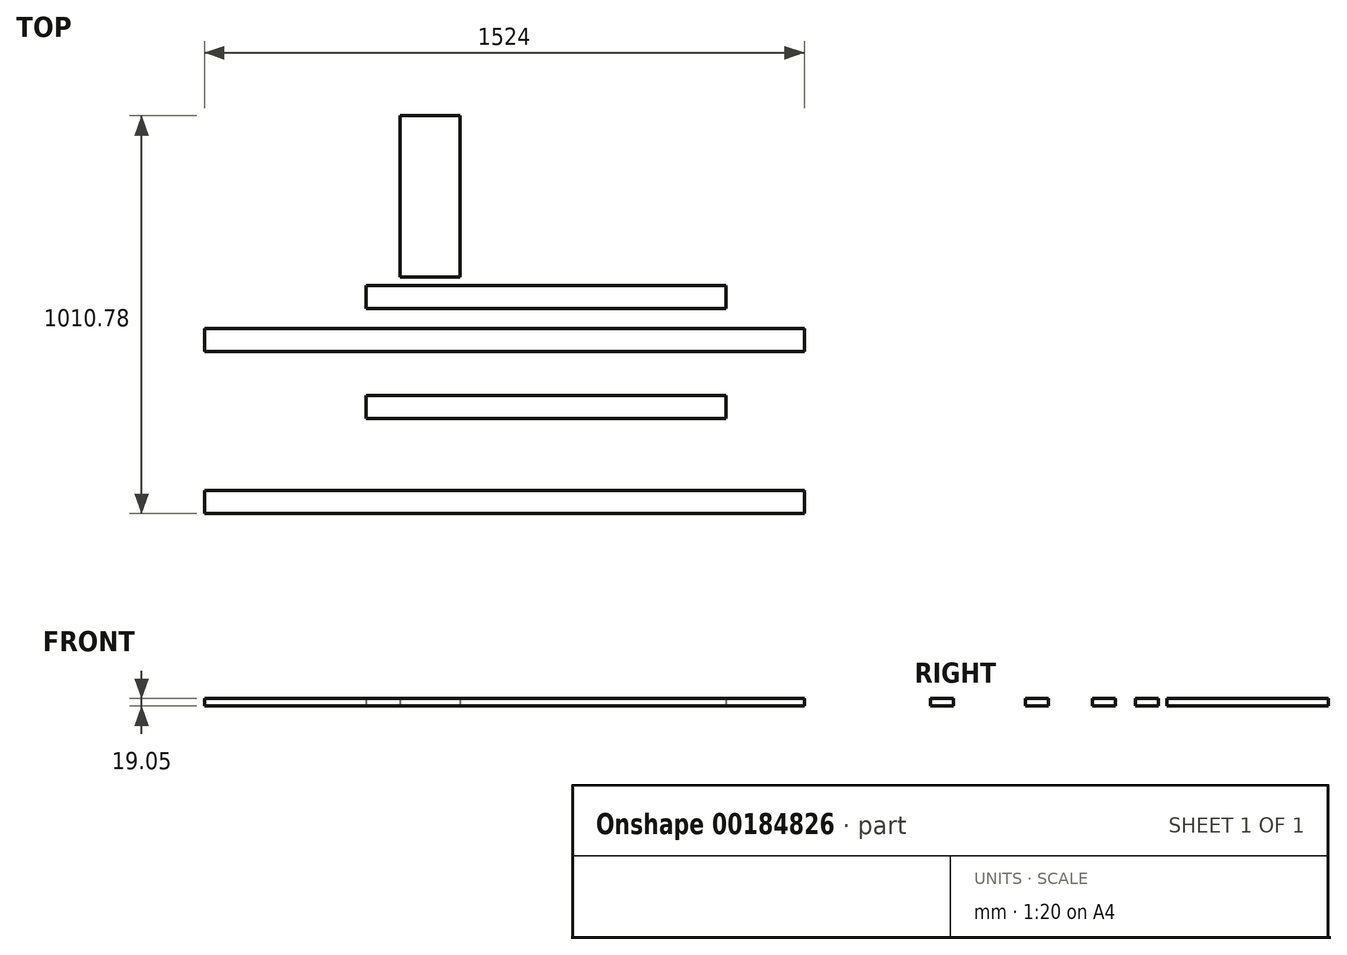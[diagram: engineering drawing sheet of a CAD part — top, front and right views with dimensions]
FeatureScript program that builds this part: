
annotation { "Feature Type Name" : "Feature", "Feature Type Description" : "" }
export const myFeature = defineFeature(function(context is Context, id is Id, definition is map)
    precondition{}
    {
        {
            var Q0;
            Q0=qCreatedBy(makeId("Top.planeOp"),FACE);
            var sketch = newSketch(context, id + "F0", { "sketchPlane" : qUnion([Q0])});
            skLineSegment(sketch, "E0.bottom", {"start": v(-772.17, 0.9) * mm, "end": v(751.83, 0.9) * mm});
            skLineSegment(sketch, "E0.top", {"start": v(-772.17, -57.84) * mm, "end": v(751.83, -57.84) * mm});
            skLineSegment(sketch, "E0.left", {"start": v(-772.17, 0.9) * mm, "end": v(-772.17, -57.84) * mm});
            skLineSegment(sketch, "E0.right", {"start": v(751.83, 0.9) * mm, "end": v(751.83, -57.84) * mm});
            skSolve(sketch);
        }
        {
            var Q0;
            Q0=makeQuery(id+"F0.imprint","IMPRINT",FACE,{"disambiguationData":[TD([[makeQuery(id+"F0.imprint","IMPRINT",EDGE,{"derivedFrom":sQuery(id+"F0.wireOp",EDGE,"E0.bottom")}),-1.0]])]});
            extrude(context, id + "F1", {"entities" : qUnion([Q0]), "depth" : 19.05 * mm});
        }
        {
            var Q0;
            Q0=qCreatedBy(makeId("Top.planeOp"),FACE);
            var sketch = newSketch(context, id + "F2", { "sketchPlane" : qUnion([Q0])});
            skLineSegment(sketch, "E1.bottom", {"start": v(-362.27, 110.11) * mm, "end": v(552.13, 110.11) * mm});
            skLineSegment(sketch, "E1.top", {"start": v(-362.27, 51.38) * mm, "end": v(552.13, 51.38) * mm});
            skLineSegment(sketch, "E1.left", {"start": v(-362.27, 110.11) * mm, "end": v(-362.27, 51.38) * mm});
            skLineSegment(sketch, "E1.right", {"start": v(552.13, 110.11) * mm, "end": v(552.13, 51.38) * mm});
            skSolve(sketch);
        }
        {
            var Q0;
            Q0=makeQuery(id+"F2.imprint","IMPRINT",FACE,{"disambiguationData":[TD([[makeQuery(id+"F2.imprint","IMPRINT",EDGE,{"derivedFrom":sQuery(id+"F2.wireOp",EDGE,"E1.bottom")}),-1.0]])]});
            extrude(context, id + "F3", {"entities" : qUnion([Q0]), "depth" : 19.05 * mm});
        }
        {
            var Q0;
            Q0=qCreatedBy(makeId("Top.planeOp"),FACE);
            var sketch = newSketch(context, id + "F4", { "sketchPlane" : qUnion([Q0])});
            skLineSegment(sketch, "E2.bottom", {"start": v(-275.76, 541.46) * mm, "end": v(-123.36, 541.46) * mm});
            skLineSegment(sketch, "E2.top", {"start": v(-275.76, 131.88) * mm, "end": v(-123.36, 131.88) * mm});
            skLineSegment(sketch, "E2.left", {"start": v(-275.76, 541.46) * mm, "end": v(-275.76, 131.88) * mm});
            skLineSegment(sketch, "E2.right", {"start": v(-123.36, 541.46) * mm, "end": v(-123.36, 131.88) * mm});
            skSolve(sketch);
        }
        {
            var Q0;
            Q0=makeQuery(id+"F4.imprint","IMPRINT",FACE,{"disambiguationData":[TD([[makeQuery(id+"F4.imprint","IMPRINT",EDGE,{"derivedFrom":sQuery(id+"F4.wireOp",EDGE,"E2.bottom")}),-1.0]])]});
            extrude(context, id + "F5", {"entities" : qUnion([Q0]), "depth" : 19.05 * mm});
        }
        {
            var Q0;
            Q0=makeQuery(id+"F1.opExtrude","SWEPT_BODY",BODY,{"disambiguationData":[OSD([sQuery(id+"F0.wireOp",EDGE,"E0.bottom"),sQuery(id+"F0.wireOp",EDGE,"E0.top"),sQuery(id+"F0.wireOp",EDGE,"E0.left"),sQuery(id+"F0.wireOp",EDGE,"E0.right")])]});
            transform(context, id + "F6", {"entities" : qUnion([Q0]), "transformType" : TransformType.TRANSLATION_3D, "dx" : 0 * mm, "dy" : -411.48 * mm, "dz" : 0 * mm, "makeCopy" : true});
        }
        {
            var Q0;
            Q0=makeQuery(id+"F3.opExtrude","SWEPT_BODY",BODY,{"disambiguationData":[OSD([sQuery(id+"F2.wireOp",EDGE,"E1.bottom"),sQuery(id+"F2.wireOp",EDGE,"E1.top"),sQuery(id+"F2.wireOp",EDGE,"E1.left"),sQuery(id+"F2.wireOp",EDGE,"E1.right")])]});
            transform(context, id + "F7", {"entities" : qUnion([Q0]), "transformType" : TransformType.TRANSLATION_3D, "dx" : 0 * mm, "dy" : -279.4 * mm, "dz" : 0 * mm, "makeCopy" : true});
        }
    });
